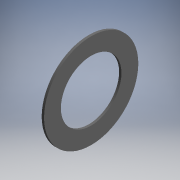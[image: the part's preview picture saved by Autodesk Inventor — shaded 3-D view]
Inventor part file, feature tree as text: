
AUTODESK INVENTOR PART (.ipt)
format: ipt  version: 2017.3 (Build 213256000, 256)  size: 95,744 bytes
history: native  units: mm (DEFAULTED — no unit token found)
features: other x7, revolve x1, sketch x1
ambient origin geometry x8: Origin, YZ Plane, XZ Plane, XY Plane, X Axis, Y Axis, Z Axis, Center Point
bodies: Solid1 (feature_tree)
feature tree (9):
  revolve  "Revolution1"  [1 undecoded]
  other  "ip_st_s1_XY"
  other  "ip_st_s1_YZ"
  other  "ip_st_s1_ZX"
  other  "ip_st_s1_X"
  other  "ip_st_s1_Y"
  other  "ip_st_s1_Z"
  other  "ip_st_s1_Center"
  sketch  "Sketch_1"  dims[d0=360.0deg d1=0.0mm]
note: 1 required parameter value undecoded (feature->parameter linkage not recoverable at this tier; creation-order binding heuristic only, values carry confidence <= 0.55)
